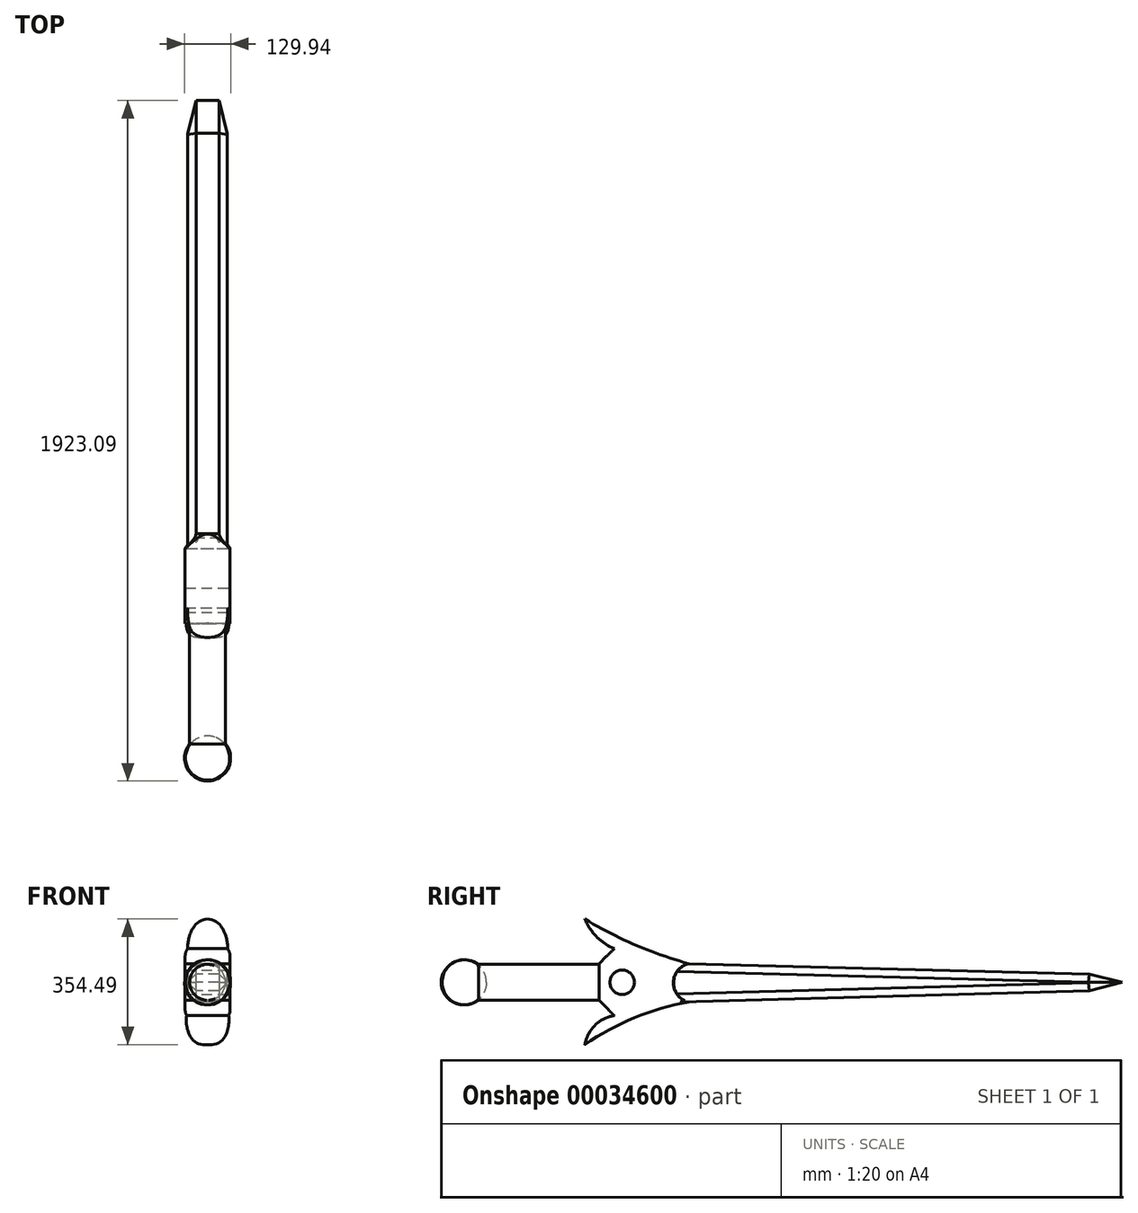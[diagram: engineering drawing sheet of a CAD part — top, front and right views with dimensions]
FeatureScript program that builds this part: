
annotation { "Feature Type Name" : "Feature", "Feature Type Description" : "" }
export const myFeature = defineFeature(function(context is Context, id is Id, definition is map)
    precondition{}
    {
        {
            var Q0;
            Q0=qCreatedBy(makeId("Front.planeOp"),FACE);
            var sketch = newSketch(context, id + "F0", { "sketchPlane" : qUnion([Q0])});
            skCircle(sketch, "E0", {"center": v(0, 0) * mm, "radius": 63.5 * mm});
            skSolve(sketch);
        }
        {
            var Q0;
            Q0 = qSketchRegion(id + "F0", true);
            extrude(context, id + "F1", {"entities" : qUnion([Q0]), "depth" : 5.08 * mm});
        }
        {
            var Q0;
            Q0=qCreatedBy(makeId("Front.planeOp"),FACE);
            var sketch = newSketch(context, id + "F2", { "sketchPlane" : qUnion([Q0])});
            skCircle(sketch, "E1", {"center": v(0, 0) * mm, "radius": 50.8 * mm});
            skSolve(sketch);
        }
        {
            var Q0;
            Q0 = qSketchRegion(id + "F2", true);
            extrude(context, id + "F3", {"entities" : qUnion([Q0]), "operationType" : NewBodyOperationType.ADD, "oppositeDirection" : true, "depth" : 381 * mm});
        }
        {
            var Q0;
            Q0=qCreatedBy(makeId("Right.planeOp"),FACE);
            var sketch = newSketch(context, id + "F4", { "sketchPlane" : qUnion([Q0])});
            skPoint(sketch, "E2.right.start.orphan", {"position": v(436.79, -0.14) * mm});
            skLineSegment(sketch, "E3", {"start": v(436.79, 0) * mm, "end": v(436.79, -0.14) * mm});
            skPoint(sketch, "E4.top.end.orphan", {"position": v(436.79, 203.2) * mm});
            skPoint(sketch, "E2.left.start.orphan", {"position": v(380.66, 0) * mm});
            skLineSegment(sketch, "E5", {"start": v(380.66, 52.77) * mm, "end": v(423.45, 95.09) * mm});
            skLineSegment(sketch, "E6", {"start": v(380.66, -50.69) * mm, "end": v(423.45, -93.96) * mm});
            skArc(sketch, "E7", {"start": v(633.36, 52.77) * mm, "mid": v(590.53, -1.4) * mm, "end": v(633.36, -55.6) * mm});
            skLineSegment(sketch, "E8", {"start": v(380.66, 52.77) * mm, "end": v(380.66, -50.69) * mm});
            skLineSegment(sketch, "E9", {"start": v(380.66, 0) * mm, "end": v(646.22, -1.4) * mm});
            skArc(sketch, "E10", {"start": v(340.64, 178.64) * mm, "mid": v(373.84, 128.74) * mm, "end": v(423.45, 95.09) * mm});
            skArc(sketch, "E11", {"start": v(340.64, 178.64) * mm, "mid": v(482.75, 105.83) * mm, "end": v(633.36, 52.77) * mm});
            skArc(sketch, "E12", {"start": v(423.45, -93.96) * mm, "mid": v(368.9, -121.62) * mm, "end": v(340.64, -175.85) * mm});
            skArc(sketch, "E13", {"start": v(633.36, -55.6) * mm, "mid": v(480.66, -100.3) * mm, "end": v(340.64, -175.85) * mm});
            skSolve(sketch);
        }
        {
            var Q0;
            Q0 = qSketchRegion(id + "F4", true);
            extrude(context, id + "F5", {"entities" : qUnion([Q0]), "operationType" : NewBodyOperationType.ADD, "depth" : 63.5 * mm});
        }
        {
            var Q0;
            Q0 = qSketchRegion(id + "F4", true);
            extrude(context, id + "F6", {"entities" : qUnion([Q0]), "operationType" : NewBodyOperationType.ADD, "oppositeDirection" : true, "depth" : 63.5 * mm});
        }
        {
            var Q0;
            Q0=qCreatedBy(makeId("Right.planeOp"),FACE);
            var sketch = newSketch(context, id + "F7", { "sketchPlane" : qUnion([Q0])});
            skArc(sketch, "E14", {"start": v(0, 63.7) * mm, "mid": v(-64.97, -0.04) * mm, "end": v(0, -63.78) * mm});
            skLineSegment(sketch, "E15", {"start": v(0, 63.7) * mm, "end": v(0, -63.78) * mm});
            skSolve(sketch);
        }
        {
            var Q0;
            Q0 = qSketchRegion(id + "F7", true);
            var Q1;
            Q1=sQuery(id+"F7.wireOp",EDGE,"E15");
            revolve(context, id + "F8", {"operationType" : NewBodyOperationType.ADD, "entities" : qUnion([Q0]), "axis" : qUnion([Q1]), "revolveType" : RevolveType.FULL});
        }
        {
            var Q0;
            Q0=qCreatedBy(makeId("Right.planeOp"),FACE);
            var sketch = newSketch(context, id + "F9", { "sketchPlane" : qUnion([Q0])});
            skArc(sketch, "E16", {"start": v(633.42, 52.59) * mm, "mid": v(591.16, -1.23) * mm, "end": v(632.68, -55.62) * mm});
            skLineSegment(sketch, "E17", {"start": v(633.42, 52.59) * mm, "end": v(1765.6, 23.57) * mm});
            skLineSegment(sketch, "E18", {"start": v(632.68, -55.62) * mm, "end": v(1765.6, -24.01) * mm});
            skLineSegment(sketch, "E19", {"start": v(1765.6, 23.57) * mm, "end": v(1858.12, 0) * mm});
            skLineSegment(sketch, "E20", {"start": v(1858.12, 0) * mm, "end": v(1765.6, -24.01) * mm});
            skLineSegment(sketch, "E21", {"start": v(1858.12, 0) * mm, "end": v(380.31, -1.62) * mm});
            skSolve(sketch);
        }
        {
            var Q0;
            Q0 = qSketchRegion(id + "F9", true);
            extrude(context, id + "F10", {"entities" : qUnion([Q0]), "operationType" : NewBodyOperationType.ADD, "depth" : 55.88 * mm});
        }
        {
            var Q0;
            Q0 = qSketchRegion(id + "F9", true);
            extrude(context, id + "F11", {"entities" : qUnion([Q0]), "operationType" : NewBodyOperationType.ADD, "oppositeDirection" : true, "depth" : 55.88 * mm});
        }
        {
            var Q0;
            Q0=makeQuery(id+"F10.opExtrude","CAP_EDGE",EDGE,{"disambiguationData":[OSD([sQuery(id+"F9.wireOp",EDGE,"E17")])],"isStart":false});
            var Q1;
            Q1=makeQuery(id+"F10.opExtrude","CAP_EDGE",EDGE,{"disambiguationData":[OSD([sQuery(id+"F9.wireOp",EDGE,"E19")])],"isStart":false});
            var Q2;
            Q2=makeQuery(id+"F10.opExtrude","CAP_EDGE",EDGE,{"disambiguationData":[OSD([sQuery(id+"F9.wireOp",EDGE,"E18")])],"isStart":false});
            var Q3;
            Q3=makeQuery(id+"F10.opExtrude","CAP_EDGE",EDGE,{"disambiguationData":[OSD([sQuery(id+"F9.wireOp",EDGE,"E20")])],"isStart":false});
            var Q4;
            Q4=makeQuery(id+"F11.opExtrude","CAP_EDGE",EDGE,{"disambiguationData":[OSD([sQuery(id+"F9.wireOp",EDGE,"E17")])],"isStart":false});
            var Q5;
            Q5=makeQuery(id+"F11.opExtrude","CAP_EDGE",EDGE,{"disambiguationData":[OSD([sQuery(id+"F9.wireOp",EDGE,"E19")])],"isStart":false});
            var Q6;
            Q6=makeQuery(id+"F11.opExtrude","CAP_EDGE",EDGE,{"disambiguationData":[OSD([sQuery(id+"F9.wireOp",EDGE,"E20")])],"isStart":false});
            var Q7;
            Q7=makeQuery(id+"F11.opExtrude","CAP_EDGE",EDGE,{"disambiguationData":[OSD([sQuery(id+"F9.wireOp",EDGE,"E18")])],"isStart":false});
            chamfer(context, id + "F12", {"entities" : qUnion([Q0, Q1, Q2, Q3, Q4, Q5, Q6, Q7]), "width" : 23.37 * mm, "tangentPropagation" : true});
        }
        {
            var Q0;
            Q0=makeQuery(id+"F6.opExtrude","CAP_EDGE",EDGE,{"disambiguationData":[OSD([sQuery(id+"F4.wireOp",EDGE,"E11")])],"isStart":false});
            fillet(context, id + "F13", {"entities" : qUnion([Q0]), "radius" : 63.5 * mm, "tangentPropagation" : true, "allowEdgeOverflow" : false});
        }
        {
            var Q0;
            Q0=makeQuery(id+"F6.opExtrude","CAP_EDGE",EDGE,{"disambiguationData":[OSD([sQuery(id+"F4.wireOp",EDGE,"E13")])],"isStart":false});
            fillet(context, id + "F14", {"entities" : qUnion([Q0]), "radius" : 50.8 * mm, "tangentPropagation" : true, "allowEdgeOverflow" : false});
        }
        {
            var Q0;
            Q0=makeQuery(id+"F5.opExtrude","CAP_EDGE",EDGE,{"disambiguationData":[OSD([sQuery(id+"F4.wireOp",EDGE,"E11")])],"isStart":false});
            fillet(context, id + "F15", {"entities" : qUnion([Q0]), "radius" : 63.5 * mm, "tangentPropagation" : true, "allowEdgeOverflow" : false});
        }
        {
            var Q0;
            Q0=makeQuery(id+"F5.opExtrude","CAP_EDGE",EDGE,{"disambiguationData":[OSD([sQuery(id+"F4.wireOp",EDGE,"E13")])],"isStart":false});
            fillet(context, id + "F16", {"entities" : qUnion([Q0]), "radius" : 50.8 * mm, "tangentPropagation" : true, "allowEdgeOverflow" : false});
        }
        {
            var Q0;
            Q0=qCreatedBy(makeId("Right.planeOp"),FACE);
            var sketch = newSketch(context, id + "F17", { "sketchPlane" : qUnion([Q0])});
            skCircle(sketch, "E22", {"center": v(446, 0) * mm, "radius": 34.6 * mm});
            skSolve(sketch);
        }
        {
            var Q0;
            Q0 = qSketchRegion(id + "F17", true);
            extrude(context, id + "F18", {"entities" : qUnion([Q0]), "operationType" : NewBodyOperationType.REMOVE, "endBound" : BoundingType.THROUGH_ALL, "oppositeDirection" : true, "depth" : 25.4 * mm});
        }
        {
            var Q0;
            Q0 = qSketchRegion(id + "F17", true);
            extrude(context, id + "F19", {"entities" : qUnion([Q0]), "operationType" : NewBodyOperationType.REMOVE, "endBound" : BoundingType.THROUGH_ALL, "depth" : 25.4 * mm});
        }
    });
